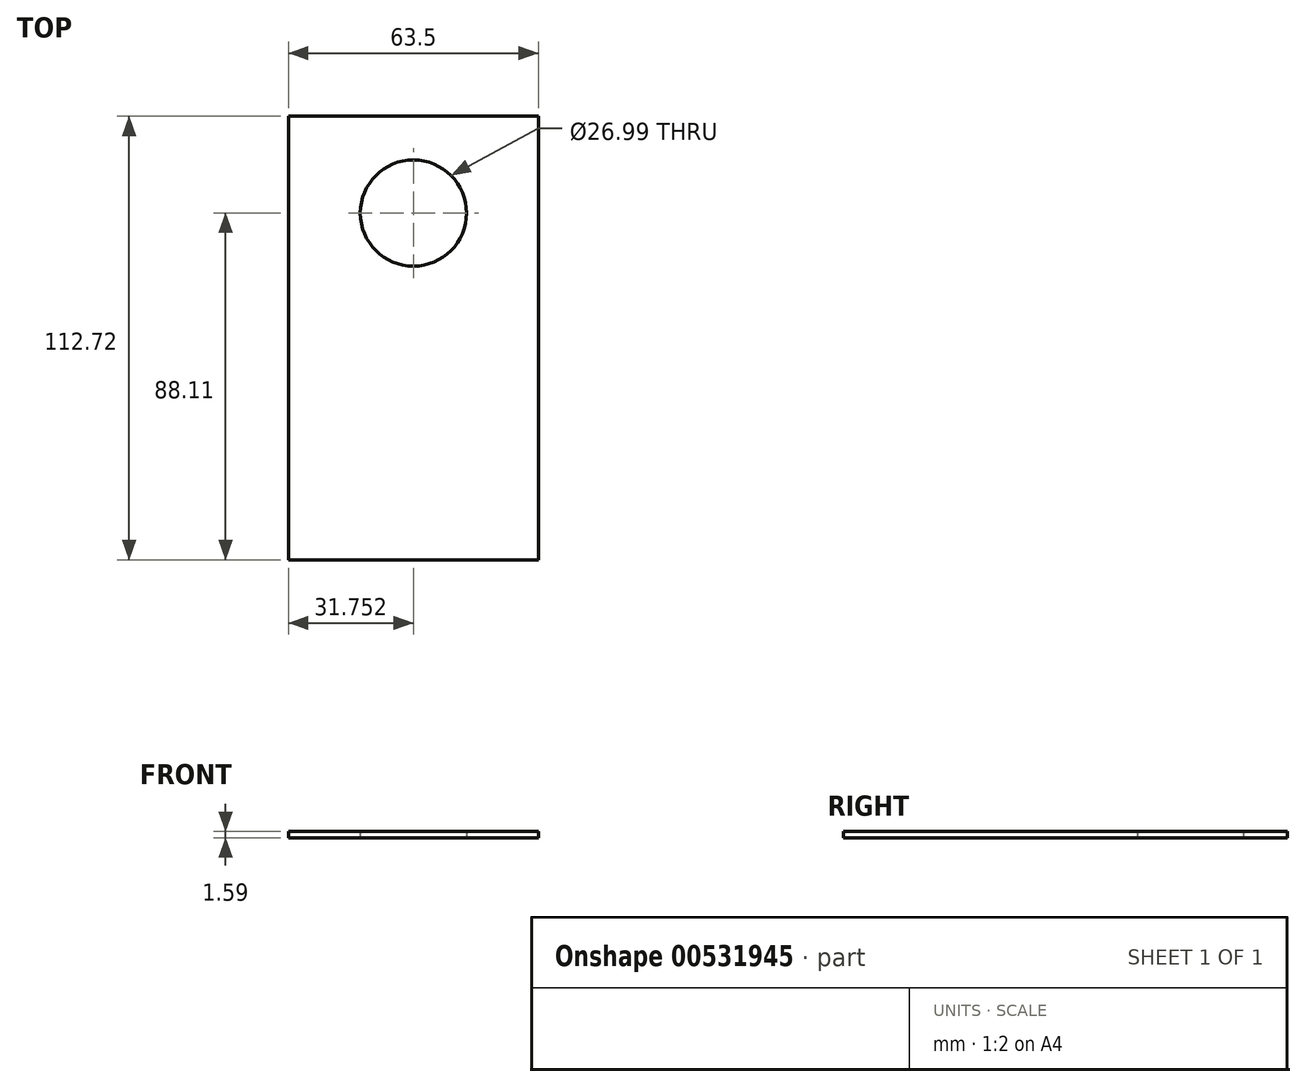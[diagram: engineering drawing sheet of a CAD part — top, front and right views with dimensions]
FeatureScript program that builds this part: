
annotation { "Feature Type Name" : "Feature", "Feature Type Description" : "" }
export const myFeature = defineFeature(function(context is Context, id is Id, definition is map)
    precondition{}
    {
        {
            var Q0;
            Q0=qCreatedBy(makeId("Top.planeOp"),FACE);
            var sketch = newSketch(context, id + "F0", { "sketchPlane" : qUnion([Q0])});
            skLineSegment(sketch, "E0.bottom", {"start": v(-38.82, 39.65) * mm, "end": v(24.68, 39.65) * mm});
            skLineSegment(sketch, "E0.top", {"start": v(-38.82, -73.07) * mm, "end": v(24.68, -73.07) * mm});
            skLineSegment(sketch, "E0.left", {"start": v(-38.82, 39.65) * mm, "end": v(-38.82, -73.07) * mm});
            skLineSegment(sketch, "E0.right", {"start": v(24.68, 39.65) * mm, "end": v(24.68, -73.07) * mm});
            skCircle(sketch, "E1", {"center": v(-7.07, 15.04) * mm, "radius": 13.5 * mm});
            skSolve(sketch);
        }
        {
            var Q0;
            Q0=makeQuery(id+"F0.imprint","IMPRINT",FACE,{"disambiguationData":[TD([[makeQuery(id+"F0.imprint","IMPRINT",EDGE,{"derivedFrom":sQuery(id+"F0.wireOp",EDGE,"E0.bottom")}),-1.0]])]});
            extrude(context, id + "F1", {"entities" : qUnion([Q0]), "depth" : 1.59 * mm, "offsetDistance" : 25.4 * mm});
        }
    });
